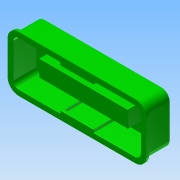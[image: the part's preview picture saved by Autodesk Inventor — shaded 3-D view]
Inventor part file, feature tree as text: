
AUTODESK INVENTOR PART (.ipt)
format: ipt  version: 2014 (Build 180170000, 170)  size: 241,152 bytes
history: native  units: in
note: dims shown in document units (in); Inventor stores cm internally (conversion verified against a paired STEP export)
features: fillet x7, extrude x5, sketch x5, mirror x4, plane x3, shell x2
ambient origin geometry x8: Origin, YZ Plane, XZ Plane, XY Plane, X Axis, Y Axis, Z Axis, Center Point
bodies: Solid1 (feature_tree)
feature tree (26):
  extrude  "Extrusion1"  Depth=0.5in
  fillet  "Fillet1"  Radius=0.47in
  shell  "Shell1"  Thickness=0.2in
  sketch  "Sketch2"  dims[d7=0.46in d8=0.2283in]
  plane  "Work Plane1"
  shell  "Shell2"  Thickness=0.1in
  extrude  "Extrusion5"  Depth=0.2283in
  plane  "Work Plane3"
  extrude  "Extrusion6"  Depth=0.47in TaperAngle=0.0deg
  plane  "Work Plane4"
  extrude  "Extrusion7"  Depth=0.01in
  fillet  "Fillet8"  Radius=0.05in
  mirror  "Mirror3"
  mirror  "Mirror4"
  fillet  "Fillet6"  Radius=0.05in
  fillet  "Fillet3"  Radius=0.445in
  fillet  "Fillet4"  Radius=0.05in
  extrude  "Extrusion2"  Depth=0.05in TaperAngle=0.0deg
  fillet  "Fillet2"  [1 undecoded]
  fillet  "Fillet7"  Radius=0.05in
  mirror  "Mirror1"
  mirror  "Mirror2"
  sketch  "Sketch1"  dims[d0=1.25in d1=0.5in d2=0.47in d3=0.0in d4=0.2in d5=0.1in]
  sketch  "Sketch4"  dims[d9=-0.033in d10=0.47in d11=0.0in]
  sketch  "Sketch5"  dims[d12=0.005in d13=0.01in d18=0.05in d23=0.05in d26=0.445in d28=0.05in]
  sketch  "Sketch6"  dims[d29=0.3in d30=0.05in d31=0.0in d32=-0.05in d33=0.05in d34=0.03in d35=0.4325in d36=0.0in d37=0.3in d38=0.8in d39=0.15in d40=0.005in d41=0.0in d42=0.005in]
note: 1 required parameter value undecoded (feature->parameter linkage not recoverable at this tier; creation-order binding heuristic only, values carry confidence <= 0.55)
